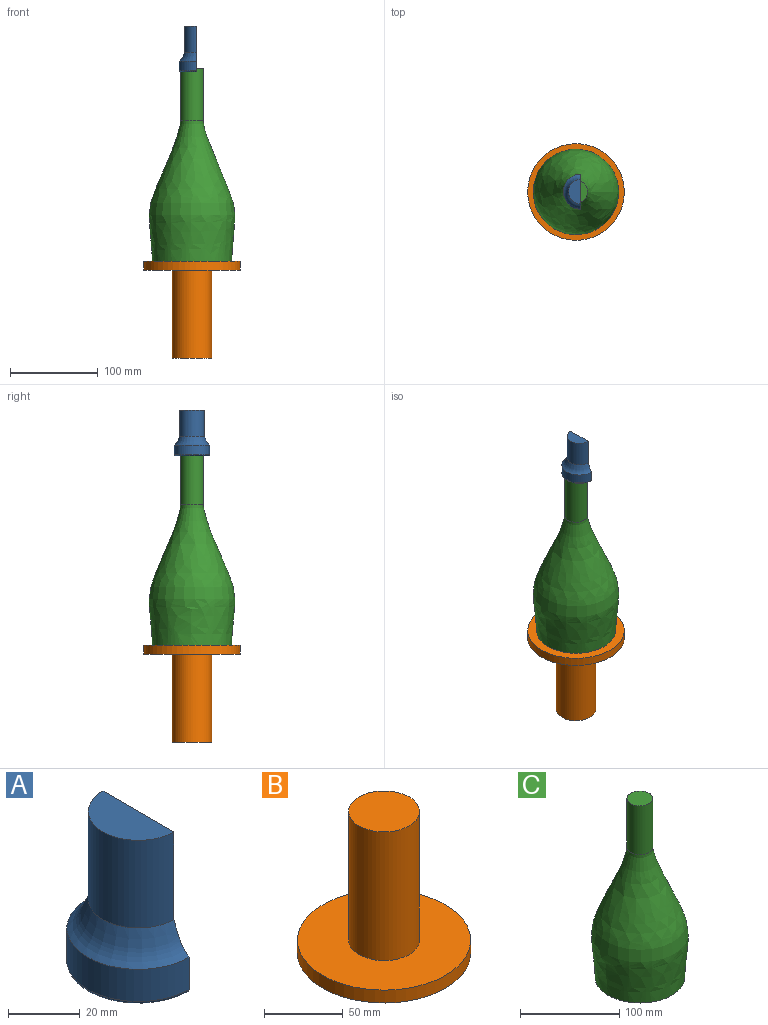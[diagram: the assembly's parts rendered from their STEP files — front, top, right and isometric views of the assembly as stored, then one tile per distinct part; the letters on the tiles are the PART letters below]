
ASSEMBLY  parts=3 mates=2
PART A: 9 faces, bbox 21.6x43.3x51.9 mm
  f0: plane 28x14mm, normal (0,0,1), area 307.9mm2, adj f1,f8
  f1: cylinder r=14mm len=30mm, axis (0,0,1), area 1319.5mm2, adj f0,f2,f8
  f2: revolved ~40x20mm, area 611.9mm2, adj f1,f3,f8
  f3: cylinder r=20mm len=40mm, axis (0,0,1), area 691.2mm2, adj f2,f6,f8
  f4: cylinder r=13mm len=26mm, axis (0,0,-1), area 612.6mm2, adj f5,f7,f8
  f5: plane 26x13mm, normal (0,0,-1), area 265.5mm2, adj f4,f8
  f6: torus R=19mm, axis (0,0,1), area 96.9mm2, adj f3,f7,f8
  f7: plane 38x19mm, normal (0,0,-1), area 301.6mm2, adj f4,f6,f8
  f8: plane 51.92x40mm, normal (1,0,0), area 1253.3mm2, adj f0,f1,f2,f3,f4,f5,f6,f7
PART B: 5 faces, bbox 110x110x110 mm
  f0: cylinder r=55mm len=110mm, axis (0,0,-1), area 3455.8mm2, adj f1,f2
  f1: plane 110x110mm, normal (0,0,1), area 7912.9mm2, adj f0,f3
  f2: plane 110x110mm, normal (0,0,-1), area 9503.3mm2, adj f0
  f3: cylinder r=22.5mm len=100mm, axis (0,0,-1), area 14137.2mm2, adj f1,f4
  f4: plane 45x45mm, normal (0,0,1), area 1590.4mm2, adj f3
PART C: 4 faces, bbox 97.6x97.6x220 mm
  f0: plane 90x90mm, normal (0,0,-1), area 6361.7mm2, adj f1
  f1: revolved ~160x97.58mm, area 37850.1mm2, adj f0,f2
  f2: cylinder r=13mm len=60mm, axis (0,0,1), area 4900.9mm2, adj f1,f3
  f3: plane 26x26mm, normal (0,0,1), area 530.9mm2, adj f2
PLACE A t=(5.52,0,326)mm
PLACE B rot(axis=(1,0,0),180deg) t=(0,0,110)mm
PLACE C t=(0,0,110)mm
MATE planar C.f2 <-> B.f0  axis (0,0,-1) through (0,0,110)mm
MATE cylindrical A.f5 <-> C.f2  axis (0,0,-1) through (0,0,341)mm
